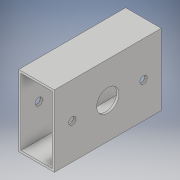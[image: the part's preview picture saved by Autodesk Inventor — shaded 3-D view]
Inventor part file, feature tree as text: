
AUTODESK INVENTOR PART (.ipt)
format: ipt  version: 2018 (Build 220112000, 112)  size: 124,928 bytes
history: native  units: in
note: dims shown in document units (in); Inventor stores cm internally (conversion verified against a paired STEP export)
features: extrude x4, sketch x4
ambient origin geometry x8: Origin, YZ Plane, XZ Plane, XY Plane, X Axis, Y Axis, Z Axis, Center Point
bodies: Solid1 (feature_tree)
feature tree (8):
  extrude  "Extrusion1"  Depth=2.0in
  extrude  "Extrusion2"  Depth=3.0in TaperAngle=0.0deg
  extrude  "Extrusion3"  Depth=0.1875in TaperAngle=0.0deg
  extrude  "Extrusion4"  Depth=2.0in TaperAngle=0.0deg
  sketch  "Sketch1"  dims[d0=1.0in d1=2.0in]
  sketch  "Sketch2"  dims[d2=0.0625in d3=3.0in d4=0.0in]
  sketch  "Sketch3"  dims[d5=0.625in d6=0.1875in d7=0.0in]
  sketch  "Sketch4"  dims[d8=0.5in d9=0.1875in d10=0.0in d11=0.5in d12=2.0in d13=0.2031in d14=2.1875in d15=0.0in]
